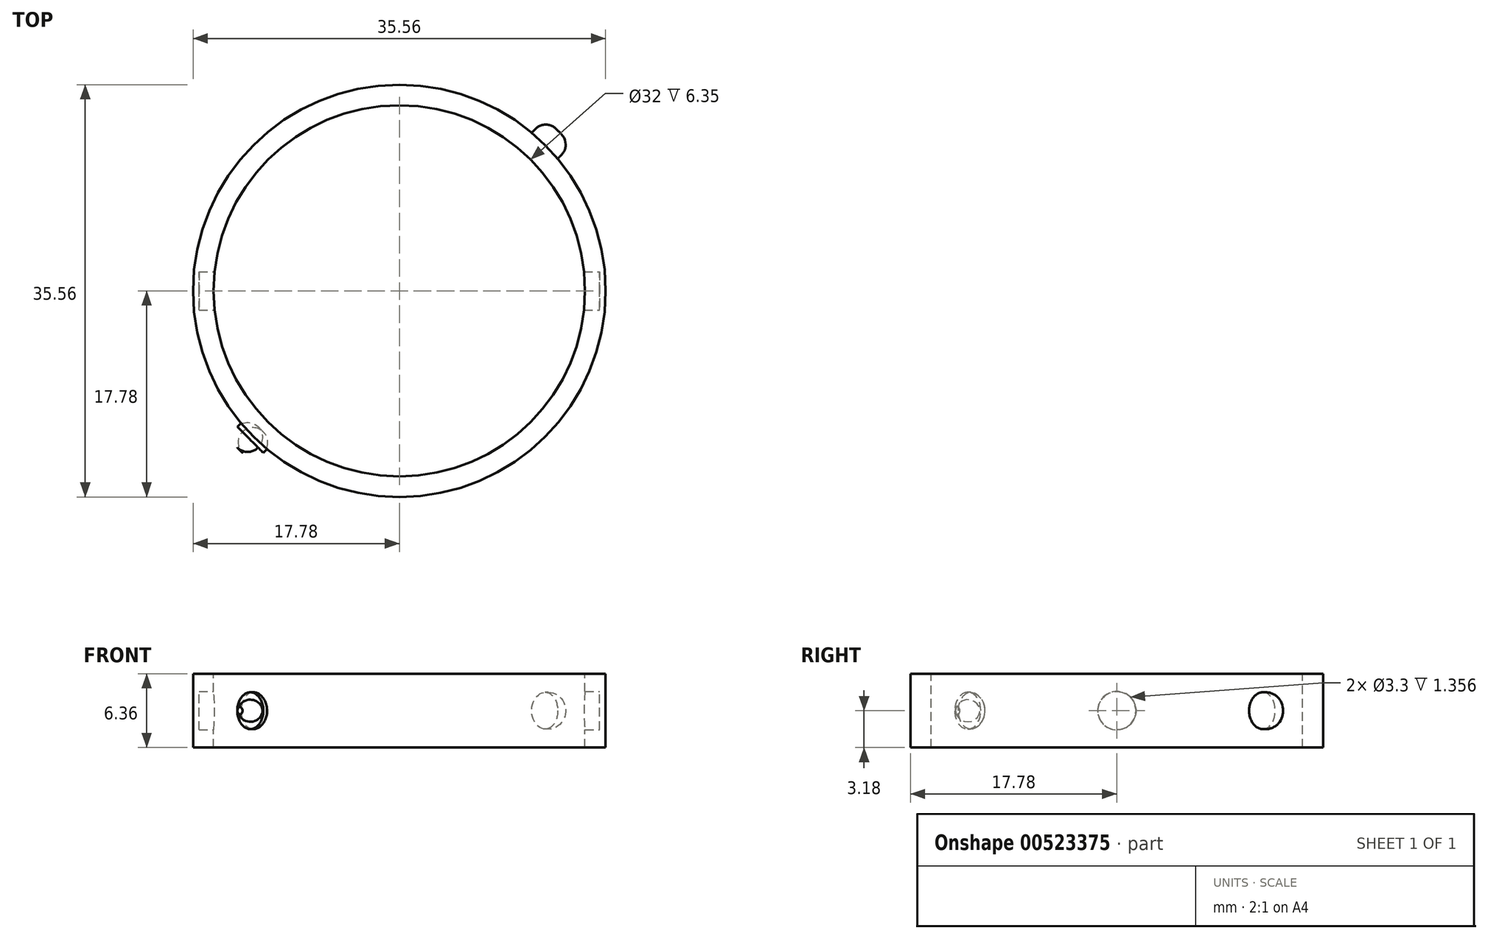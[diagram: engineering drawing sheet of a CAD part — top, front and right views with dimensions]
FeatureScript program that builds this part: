
annotation { "Feature Type Name" : "Feature", "Feature Type Description" : "" }
export const myFeature = defineFeature(function(context is Context, id is Id, definition is map)
    precondition{}
    {
        {
            var Q0;
            Q0=qCreatedBy(makeId("Right.planeOp"),FACE);
            var Q1;
            Q1=qCreatedBy(makeId("Front.planeOp"),FACE);
            cPlane(context, id + "F0", {"entities" : qUnion([Q0, Q1]), "cplaneType" : CPlaneType.MID_PLANE, "offset" : 25.4 * mm, "oppositeDirection" : true, "width" : 152.4 * mm, "height" : 152.4 * mm});
        }
        {
            var Q0;
            Q0=qCreatedBy(makeId("Top.planeOp"),FACE);
            var sketch = newSketch(context, id + "F1", { "sketchPlane" : qUnion([Q0])});
            skCircle(sketch, "E0", {"center": v(0, 0) * mm, "radius": 17.78 * mm});
            skSolve(sketch);
        }
        {
            var Q0;
            Q0=makeQuery(id+"F1.imprint","IMPRINT",FACE,{"disambiguationData":[TD([[makeQuery(id+"F1.imprint","IMPRINT",EDGE,{"derivedFrom":sQuery(id+"F1.wireOp",EDGE,"E0")}),1.0]])]});
            extrude(context, id + "F2", {"entities" : qUnion([Q0]), "endBound" : BoundingType.SYMMETRIC, "depth" : 6.35 * mm, "offsetDistance" : 25.4 * mm});
        }
        {
            var Q0;
            Q0=qCreatedBy(makeId("Right.planeOp"),FACE);
            var sketch = newSketch(context, id + "F3", { "sketchPlane" : qUnion([Q0])});
            skCircle(sketch, "E1", {"center": v(0, 0) * mm, "radius": 1.65 * mm});
            skSolve(sketch);
        }
        {
            var Q0;
            Q0=makeQuery(id+"F3.imprint","IMPRINT",FACE,{"disambiguationData":[TD([[makeQuery(id+"F3.imprint","IMPRINT",EDGE,{"derivedFrom":sQuery(id+"F3.wireOp",EDGE,"E1")}),1.0]])]});
            extrude(context, id + "F4", {"entities" : qUnion([Q0]), "operationType" : NewBodyOperationType.REMOVE, "endBound" : BoundingType.SYMMETRIC, "oppositeDirection" : true, "depth" : 34.54 * mm, "offsetDistance" : 25.4 * mm, "hasSecondDirection" : true, "secondDirectionOppositeDirection" : false, "secondDirectionDepth" : 14.73 * mm});
        }
        {
            var Q0;
            Q0=qCreatedBy(id+"F0.planeOp",FACE);
            var sketch = newSketch(context, id + "F5", { "sketchPlane" : qUnion([Q0])});
            skCircle(sketch, "E2", {"center": v(0, 0) * mm, "radius": 1.59 * mm});
            skSolve(sketch);
        }
        {
            var Q0;
            Q0=qSketchRegion(id+"F5",true);
            extrude(context, id + "F6", {"entities" : qUnion([Q0]), "operationType" : NewBodyOperationType.ADD, "endBound" : BoundingType.SYMMETRIC, "depth" : 38.86 * mm, "offsetDistance" : 25.4 * mm});
        }
        {
            var Q0;
            Q0=makeQuery(id+"F2.opExtrude","CAP_FACE",FACE,{"disambiguationData":[OSD([sQuery(id+"F1.wireOp",EDGE,"E0")])],"isStart":false});
            var sketch = newSketch(context, id + "F7", { "sketchPlane" : qUnion([Q0])});
            skCircle(sketch, "E3", {"center": v(0, 0) * mm, "radius": 16 * mm});
            skSolve(sketch);
        }
        {
            var Q0;
            Q0=qSketchRegion(id+"F7",true);
            extrude(context, id + "F8", {"entities" : qUnion([Q0]), "operationType" : NewBodyOperationType.REMOVE, "endBound" : BoundingType.THROUGH_ALL, "oppositeDirection" : true, "depth" : 25.4 * mm, "offsetDistance" : 25.4 * mm});
        }
        {
            var Q0;
            Q0=makeQuery(id+"F6.opExtrude","CAP_EDGE",EDGE,{"disambiguationData":[OSD([sQuery(id+"F5.wireOp",EDGE,"E2")])],"isStart":false});
            var Q1;
            Q1=makeQuery(id+"F6.opExtrude","CAP_EDGE",EDGE,{"disambiguationData":[OSD([sQuery(id+"F5.wireOp",EDGE,"E2")])],"isStart":true});
            fillet(context, id + "F9", {"entities" : qUnion([Q0, Q1]), "radius" : 1.27 * mm, "tangentPropagation" : true, "allowEdgeOverflow" : false});
        }
    });
